# Revit family: mcr FID-НО-К1-D
name_source: partatom
category: Арматура воздуховодов
revit_build: Autodesk Revit 2016 (Build: 20150714_1515(x64)
units: mm (PartAtom-declared; Revit-internal decimal feet)

## family parameters
Всегда вертикально = Да
На основе рабочей плоскости = Нет
Общий = Да
При загрузке вырезать с полостями = Нет
Размер круглого соединителя = Использовать диаметр
Тип детали = Вставляется

## types (3) — shared parameters
P = 1.2000 кг/куб. м
Материал клапана = <По категории>
Таблица_120 = mcr FID-120-НО-К1-D
Таблица_60 = mcr FID-60-НО-К1-D
Таблица_90 = mcr FID-90-НО-К1-D
Толщина заслонки = 10 мм
Толщина стенки = 3 мм
ЭМ230 = Нет
ЭМ24 = Нет
zero-valued in all types: ADSK_Масса

## per-type parameters (varying)
| type | Таблица_выбора |
| EI60 | mcr FID-60-НО-К1-D |
| EI90 | mcr FID-90-НО-К1-D |
| EI120 | mcr FID-120-НО-К1-D |

note: column(s) folded — value = type name in every type: EI

## geometry (parser evidence)
native form markers: Blend x2
no freeform markers — native parametric forms only
